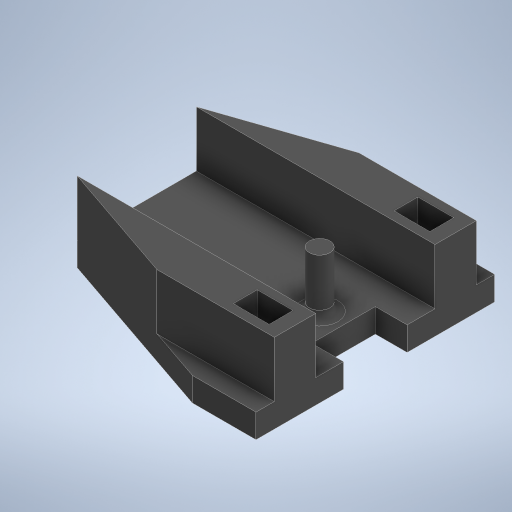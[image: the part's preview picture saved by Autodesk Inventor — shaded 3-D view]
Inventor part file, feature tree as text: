
AUTODESK INVENTOR PART (.ipt)
format: ipt  version: 2024.2 (Build 282272000, 272)  size: 323,584 bytes
history: native  units: mm
features: extrude x4, sketch x4, fillet x1
ambient origin geometry x8: Origin, YZ Plane, XZ Plane, XY Plane, X Axis, Y Axis, Z Axis, Center Point
bodies: Solid1 (feature_tree)
feature tree (9):
  extrude  "Extrusion1"  Depth=8.0mm
  extrude  "Extrusion2"  Depth=3.0mm
  extrude  "Extrusion3"  Depth=17.2mm
  extrude  "Extrusion4"  Depth=1.75mm
  fillet  "Fillet1"  Radius=15.0mm
  sketch  "Sketch1"  dims[d0=30.0mm d1=8.0mm]
  sketch  "Sketch2"  dims[d2=4.5mm d3=3.0mm]
  sketch  "Sketch3"  dims[d4=3.0mm d5=17.2mm]
  sketch  "Sketch4"  dims[d6=3.4mm d7=1.75mm d8=15.0mm d10=7.5mm d11=22.0mm d12=22.0mm d13=3.0mm d14=0.0mm d17=2.6mm d21=1.1mm d22=1.1mm d23=15.0mm d24=7.0mm d25=7.0mm d26=0.0mm d27=0.0mm d28=0.0mm d29=3.0mm d30=8.0mm d31=3.5mm d32=0.0mm d33=0.0mm d34=1.0mm]
